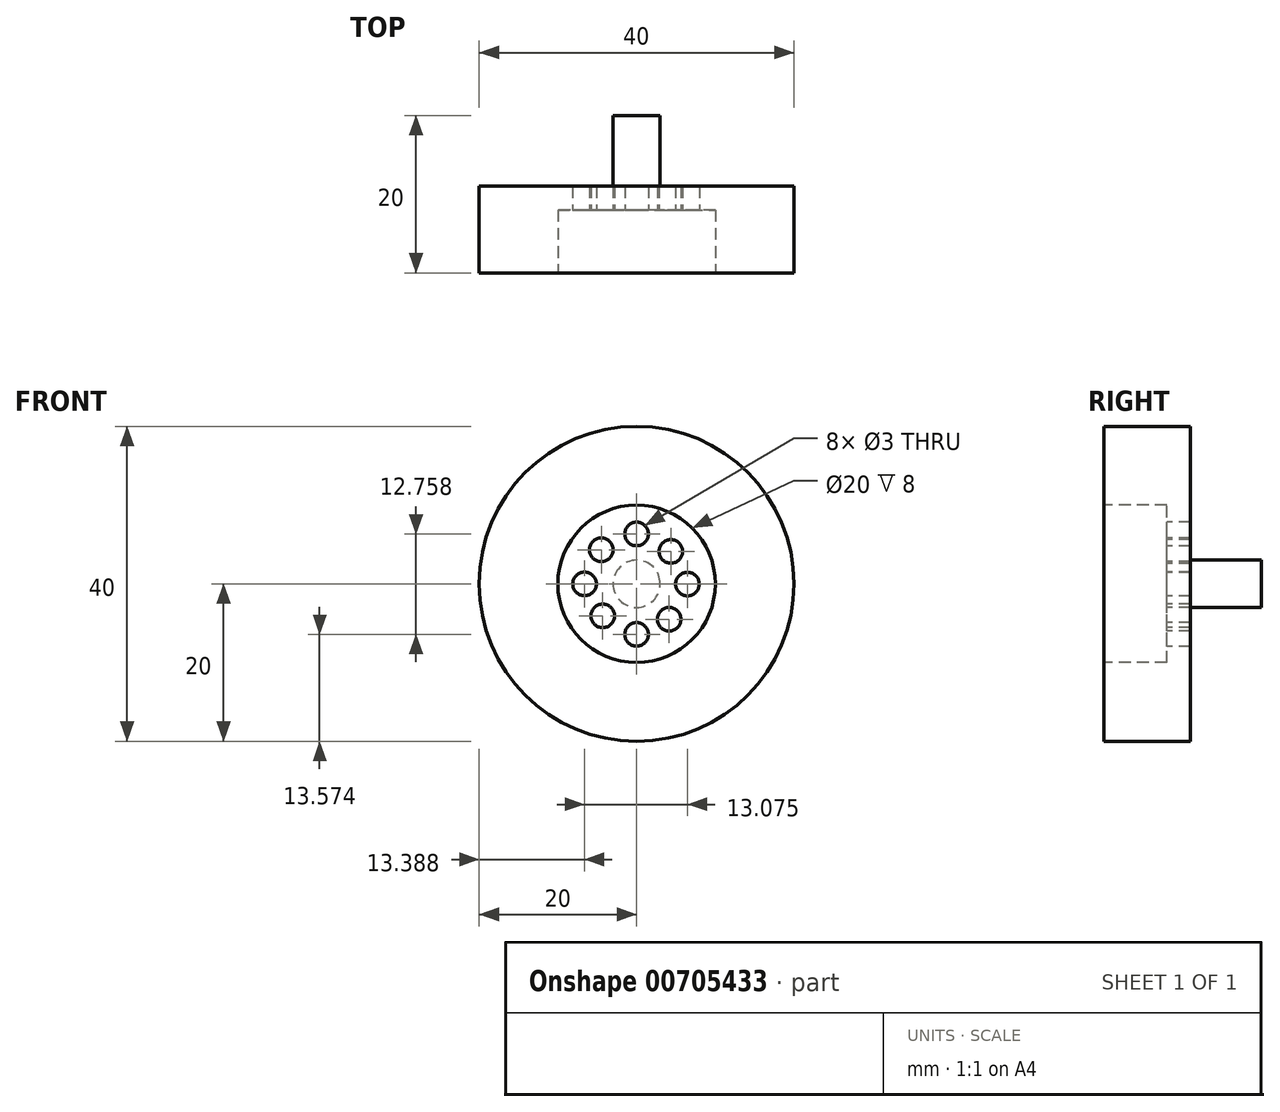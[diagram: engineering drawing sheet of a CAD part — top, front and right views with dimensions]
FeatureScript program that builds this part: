
annotation { "Feature Type Name" : "Feature", "Feature Type Description" : "" }
export const myFeature = defineFeature(function(context is Context, id is Id, definition is map)
    precondition{}
    {
        {
            var Q0;
            Q0=qCreatedBy(makeId("Front.planeOp"),FACE);
            var sketch = newSketch(context, id + "F0", { "sketchPlane" : qUnion([Q0])});
            skCircle(sketch, "E0", {"center": v(0, 0) * mm, "radius": 3 * mm});
            skSolve(sketch);
        }
        {
            var Q0;
            Q0=makeQuery(id+"F0.imprint","IMPRINT",FACE,{"disambiguationData":[TD([[makeQuery(id+"F0.imprint","IMPRINT",EDGE,{"derivedFrom":sQuery(id+"F0.wireOp",EDGE,"E0")}),1.0]])]});
            extrude(context, id + "F1", {"entities" : qUnion([Q0]), "oppositeDirection" : true, "depth" : 9 * mm, "offsetDistance" : 25 * mm});
        }
        {
            var Q0;
            Q0=makeQuery(id+"F1.opExtrude","CAP_FACE",FACE,{"disambiguationData":[OSD([sQuery(id+"F0.wireOp",EDGE,"E0")])],"isStart":true});
            var sketch = newSketch(context, id + "F2", { "sketchPlane" : qUnion([Q0])});
            skCircle(sketch, "E1", {"center": v(0, 0) * mm, "radius": 20 * mm});
            skSolve(sketch);
        }
        {
            var Q0;
            Q0=makeQuery(id+"F2.imprint","IMPRINT",FACE,{"disambiguationData":[TD([[makeQuery(id+"F2.imprint","IMPRINT",EDGE,{"derivedFrom":makeQuery(id+"F1.opExtrude","CAP_EDGE",EDGE,{"disambiguationData":[OSD([sQuery(id+"F0.wireOp",EDGE,"E0")])],"isStart":true})}),1.0]])]});
            extrude(context, id + "F3", {"entities" : qUnion([Q0]), "operationType" : NewBodyOperationType.ADD, "depth" : 9.5 * mm, "offsetDistance" : 25 * mm});
        }
        {
            var Q0;
            Q0 = qSketchRegion(id + "F2", true);
            extrude(context, id + "F4", {"entities" : qUnion([Q0]), "operationType" : NewBodyOperationType.ADD, "depth" : 11 * mm, "offsetDistance" : 25 * mm});
        }
        {
            var Q0;
            Q0=makeQuery(id+"F4.opExtrude","CAP_FACE",FACE,{"disambiguationData":[OSD([sQuery(id+"F2.wireOp",EDGE,"E1")])],"isStart":false});
            var sketch = newSketch(context, id + "F5", { "sketchPlane" : qUnion([Q0])});
            skCircle(sketch, "E2", {"center": v(0, 0) * mm, "radius": 10 * mm});
            skSolve(sketch);
        }
        {
            var Q0;
            Q0=makeQuery(id+"F5.imprint","IMPRINT",FACE,{"disambiguationData":[TD([[makeQuery(id+"F5.imprint","IMPRINT",EDGE,{"derivedFrom":sQuery(id+"F5.wireOp",EDGE,"E2")}),1.0]])]});
            extrude(context, id + "F6", {"entities" : qUnion([Q0]), "operationType" : NewBodyOperationType.REMOVE, "oppositeDirection" : true, "depth" : 8 * mm, "offsetDistance" : 25 * mm});
        }
        {
            var Q0;
            Q0=makeQuery(id+"F6.boolean.opBoolean","COPY",FACE,{"derivedFrom":makeQuery(id+"F6.opExtrude","CAP_FACE",FACE,{"disambiguationData":[OSD([sQuery(id+"F5.wireOp",EDGE,"E2")])],"isStart":false})});
            var sketch = newSketch(context, id + "F7", { "sketchPlane" : qUnion([Q0])});
            skCircle(sketch, "E3", {"center": v(0, 6.33) * mm, "radius": 1.5 * mm});
            skCircle(sketch, "E4", {"center": v(6.46, -0.04) * mm, "radius": 1.5 * mm});
            skCircle(sketch, "E5", {"center": v(4.14, -4.5) * mm, "radius": 1.5 * mm});
            skCircle(sketch, "E6", {"center": v(0, -6.43) * mm, "radius": 1.5 * mm});
            skCircle(sketch, "E7", {"center": v(-4.3, -4.07) * mm, "radius": 1.5 * mm});
            skCircle(sketch, "E8", {"center": v(-6.61, -0.01) * mm, "radius": 1.5 * mm});
            skCircle(sketch, "E9", {"center": v(-4.48, 4.32) * mm, "radius": 1.5 * mm});
            skCircle(sketch, "E10", {"center": v(4.35, 4.12) * mm, "radius": 1.5 * mm});
            skSolve(sketch);
        }
        {
            var Q0;
            Q0=makeQuery(id+"F7.imprint","IMPRINT",FACE,{"disambiguationData":[TD([[makeQuery(id+"F7.imprint","IMPRINT",EDGE,{"derivedFrom":sQuery(id+"F7.wireOp",EDGE,"E4")}),1.0]])]});
            var Q1;
            Q1=makeQuery(id+"F7.imprint","IMPRINT",FACE,{"disambiguationData":[TD([[makeQuery(id+"F7.imprint","IMPRINT",EDGE,{"derivedFrom":sQuery(id+"F7.wireOp",EDGE,"E10")}),1.0]])]});
            var Q2;
            Q2=makeQuery(id+"F7.imprint","IMPRINT",FACE,{"disambiguationData":[TD([[makeQuery(id+"F7.imprint","IMPRINT",EDGE,{"derivedFrom":sQuery(id+"F7.wireOp",EDGE,"E3")}),1.0]])]});
            var Q3;
            Q3=makeQuery(id+"F7.imprint","IMPRINT",FACE,{"disambiguationData":[TD([[makeQuery(id+"F7.imprint","IMPRINT",EDGE,{"derivedFrom":sQuery(id+"F7.wireOp",EDGE,"E9")}),1.0]])]});
            var Q4;
            Q4=makeQuery(id+"F7.imprint","IMPRINT",FACE,{"disambiguationData":[TD([[makeQuery(id+"F7.imprint","IMPRINT",EDGE,{"derivedFrom":sQuery(id+"F7.wireOp",EDGE,"E8")}),1.0]])]});
            var Q5;
            Q5=makeQuery(id+"F7.imprint","IMPRINT",FACE,{"disambiguationData":[TD([[makeQuery(id+"F7.imprint","IMPRINT",EDGE,{"derivedFrom":sQuery(id+"F7.wireOp",EDGE,"E7")}),1.0]])]});
            var Q6;
            Q6=makeQuery(id+"F7.imprint","IMPRINT",FACE,{"disambiguationData":[TD([[makeQuery(id+"F7.imprint","IMPRINT",EDGE,{"derivedFrom":sQuery(id+"F7.wireOp",EDGE,"E6")}),1.0]])]});
            var Q7;
            Q7=makeQuery(id+"F7.imprint","IMPRINT",FACE,{"disambiguationData":[TD([[makeQuery(id+"F7.imprint","IMPRINT",EDGE,{"derivedFrom":sQuery(id+"F7.wireOp",EDGE,"E5")}),1.0]])]});
            var Q8;
            Q8=sQuery(id+"F7.wireOp",EDGE,"E4");
            var Q9;
            Q9=sQuery(id+"F7.wireOp",EDGE,"E10");
            var Q10;
            Q10=sQuery(id+"F7.wireOp",EDGE,"E3");
            var Q11;
            Q11=sQuery(id+"F7.wireOp",EDGE,"E9");
            var Q12;
            Q12=sQuery(id+"F7.wireOp",EDGE,"E8");
            var Q13;
            Q13=sQuery(id+"F7.wireOp",EDGE,"E7");
            var Q14;
            Q14=sQuery(id+"F7.wireOp",EDGE,"E6");
            var Q15;
            Q15=sQuery(id+"F7.wireOp",EDGE,"E5");
            extrude(context, id + "F8", {"entities" : qUnion([Q0, Q1, Q2, Q3, Q4, Q5, Q6, Q7]), "operationType" : NewBodyOperationType.REMOVE, "surfaceEntities" : qUnion([Q8, Q9, Q10, Q11, Q12, Q13, Q14, Q15]), "oppositeDirection" : true, "depth" : 8 * mm, "offsetDistance" : 25 * mm});
        }
    });
